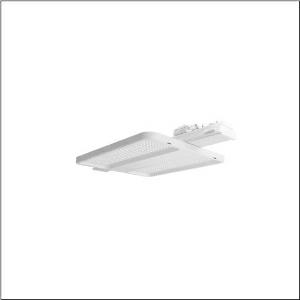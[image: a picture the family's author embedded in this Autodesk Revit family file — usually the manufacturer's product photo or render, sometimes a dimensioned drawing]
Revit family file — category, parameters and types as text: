
# Revit family: highbay_21_fur_licross_r__tragschiene_midi_52hn12da4lla_f223
name_source: partatom
category: Lighting Fixtures
units: mm (PartAtom-declared; Revit-internal decimal feet)

## family parameters
Cut with Voids When Loaded = No
Host = Face
Light Source = No
Part Type = Normal
Room Calculation Point = No
Round Connector Dimension = Use Diameter
Shared = No

## types (1)
- --- (1 x LED, 26500 lm, 142.6 W, 4000K)
    Apparent Load = 143 VA
    CIE Flux Codes = 90 98 100 100 100
    Color Rendering = 80
    Color Temperature = 4000K
    Default Elevation = 1800 mm
    Description = Highbay 21 for Licross® trunking rail midi, high bay luminaire, primary light control with lens, of PMMA, primary optical cover: cover, of PMMA, light emission: direct distribution, primary light characteristic: symmetric, LED, rated luminous flux: 26.500lm, luminous efficacy: 186lm/W, light colour: 840, colour temperature: 4000K, control gear: DALI 2, with plug, 5-pole, with phase selection, mains connection: 230..240V, AC, 50/60Hz, rated input power: 142.6W, housing frame, of high-performance plastic PA6, matt traffic white (RAL 9016), length: 750mm, width: 442mm, height: 71mm, lever catch, fixing on rail side, of steel, galvanised, white, blank cover, of PC/ABS, traffic white (RAL 9016), protection rating (complete): IP64, insulation class (complete): insulation class I (protective earthing), certification: CE, ENEC, VDE, UKCA, protection symbol: D, impact resistance: IK07, permissible operating ambient temperature: -40..+55°C, LABS conformity tested according to VDMA 24364:2018-05, corresponds to IFS (International Featured Standards) requirements for safety and quality in the food industry, packaging unit: 1 piece
    Height = 72 mm  [stored 0.23622 ft]
    Lamp = 1 x LED
    Lamp Light Flux = 26500 lm
    Lamp Power = 142.6 W
    Lamp count = 1
    Length = 474 mm
    Luminous efficacy = 186 lm/W
    Manufacturer = Siteco
    ModVariant = No
    Model = 52HN12DA4LLA
    Mounting Place = Ceiling
    Mounting Type = Pendant
    Number of Poles = 1
    OnlyDefault = Yes
    Power Factor = 1
    Product Name = Highbay 21 für Licross® Tragschiene midi
    Product group = high bay luminaire
    ProductGroupID = 901
    Protection Class = Protection class I
    Protection Degree = IP 64
    RLX_Detail_Level = 1
    RLX_Emergency_Light_Flux = 0 lm
    RLX_Emergency_Type = 0
    RLX_Emergency_Type_DB = No
    RlxData = <blob elided: 17689 chars, md5=2c2c0689>
    Socket = socket
    Standby Power = 0 W
    System Light Flux = 26499 lm
    System Power = 143 W
    Type Comments = factory setting: luminous flux: 100 % | dim-lin: 254 | 652 mA
    Type Image = l_1363258.jpg
    URL = http://relux.com
    VarID = @adj_000475
    Voltage = 0 V
    Weight = 0.00 kg
    Width = 442 mm

note: [stored X ft] marks values corroborated as IEEE doubles in the binary element streams (Revit-internal decimal feet)

## geometry (parser evidence)
native form markers: Blend x4, Sweep x11
no freeform markers — native parametric forms only
